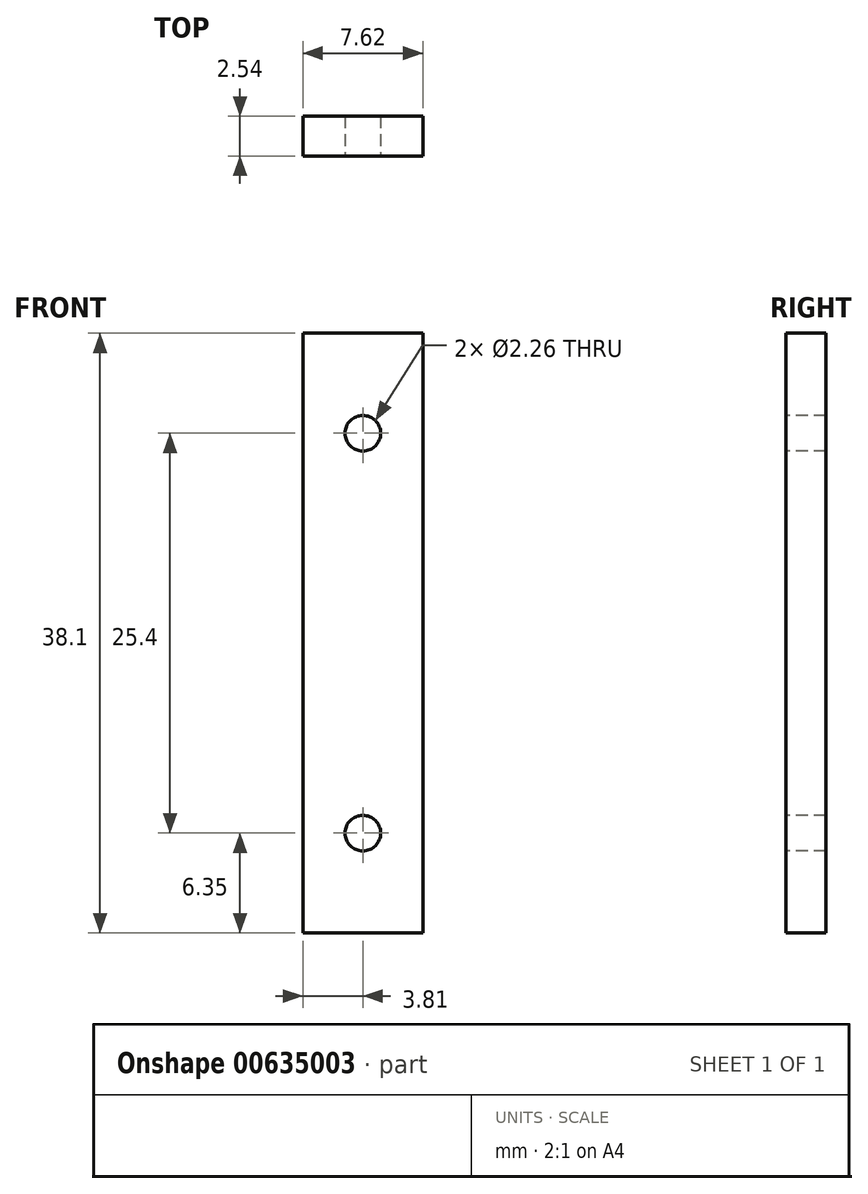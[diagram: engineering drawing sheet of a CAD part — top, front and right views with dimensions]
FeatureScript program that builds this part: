
annotation { "Feature Type Name" : "Feature", "Feature Type Description" : "" }
export const myFeature = defineFeature(function(context is Context, id is Id, definition is map)
    precondition{}
    {
        {
            var Q0;
            Q0=qCreatedBy(makeId("Front.planeOp"),FACE);
            var sketch = newSketch(context, id + "F0", { "sketchPlane" : qUnion([Q0])});
            skLineSegment(sketch, "E0.bottom", {"start": v(0, 0) * mm, "end": v(7.62, 0) * mm});
            skLineSegment(sketch, "E0.top", {"start": v(0, 38.1) * mm, "end": v(7.62, 38.1) * mm});
            skLineSegment(sketch, "E0.left", {"start": v(0, 0) * mm, "end": v(0, 38.1) * mm});
            skLineSegment(sketch, "E0.right", {"start": v(7.62, 0) * mm, "end": v(7.62, 38.1) * mm});
            skSolve(sketch);
        }
        {
            var Q0;
            Q0=makeQuery(id+"F0.imprint","IMPRINT",FACE,{"disambiguationData":[TD([[makeQuery(id+"F0.imprint","IMPRINT",EDGE,{"derivedFrom":sQuery(id+"F0.wireOp",EDGE,"E0.bottom")}),1.0]])]});
            extrude(context, id + "F1", {"entities" : qUnion([Q0]), "depth" : 2.54 * mm, "offsetDistance" : 25.4 * mm});
        }
        {
            var Q0;
            Q0=makeQuery(id+"F1.opExtrude","CAP_FACE",FACE,{"disambiguationData":[OSD([sQuery(id+"F0.wireOp",EDGE,"E0.bottom"),sQuery(id+"F0.wireOp",EDGE,"E0.top"),sQuery(id+"F0.wireOp",EDGE,"E0.left"),sQuery(id+"F0.wireOp",EDGE,"E0.right")])],"isStart":false});
            var sketch = newSketch(context, id + "F2", { "sketchPlane" : qUnion([Q0])});
            skLineSegment(sketch, "E1", {"start": v(3.8, 31.75) * mm, "end": v(3.81, 6.35) * mm});
            skSolve(sketch);
        }
        {
            var Q0;
            Q0=sQuery(id+"F2.wireOp",VERTEX,"E1.start");
            var Q1;
            Q1=sQuery(id+"F2.wireOp",VERTEX,"E1.end");
            var Q2;
            Q2=makeQuery(id+"F1.opExtrude","SWEPT_BODY",BODY,{"disambiguationData":[OSD([sQuery(id+"F0.wireOp",EDGE,"E0.bottom"),sQuery(id+"F0.wireOp",EDGE,"E0.top"),sQuery(id+"F0.wireOp",EDGE,"E0.left"),sQuery(id+"F0.wireOp",EDGE,"E0.right")])]});
            hole(context, id + "F3", {"style" : HoleStyle.SIMPLE, "endStyle" : HoleEndStyle.THROUGH, "standardTappedOrClearance" : lookupTablePath({ "standard" : "ANSI", "fit" : "Close", "size" : "#2", "type" : "Clearance" }), "standardBlindInLast" : lookupTablePath({ "fit" : "Close", "standard" : "ANSI", "size" : "#2", "type" : "Clearance" }), "holeDiameter" : 2.26 * mm, "majorDiameter" : 2.18 * mm, "tappedDepth" : 3.8 * mm, "tapClearance" : 3, "locations" : qUnion([Q0, Q1]), "scope" : qUnion([Q2])});
        }
    });
